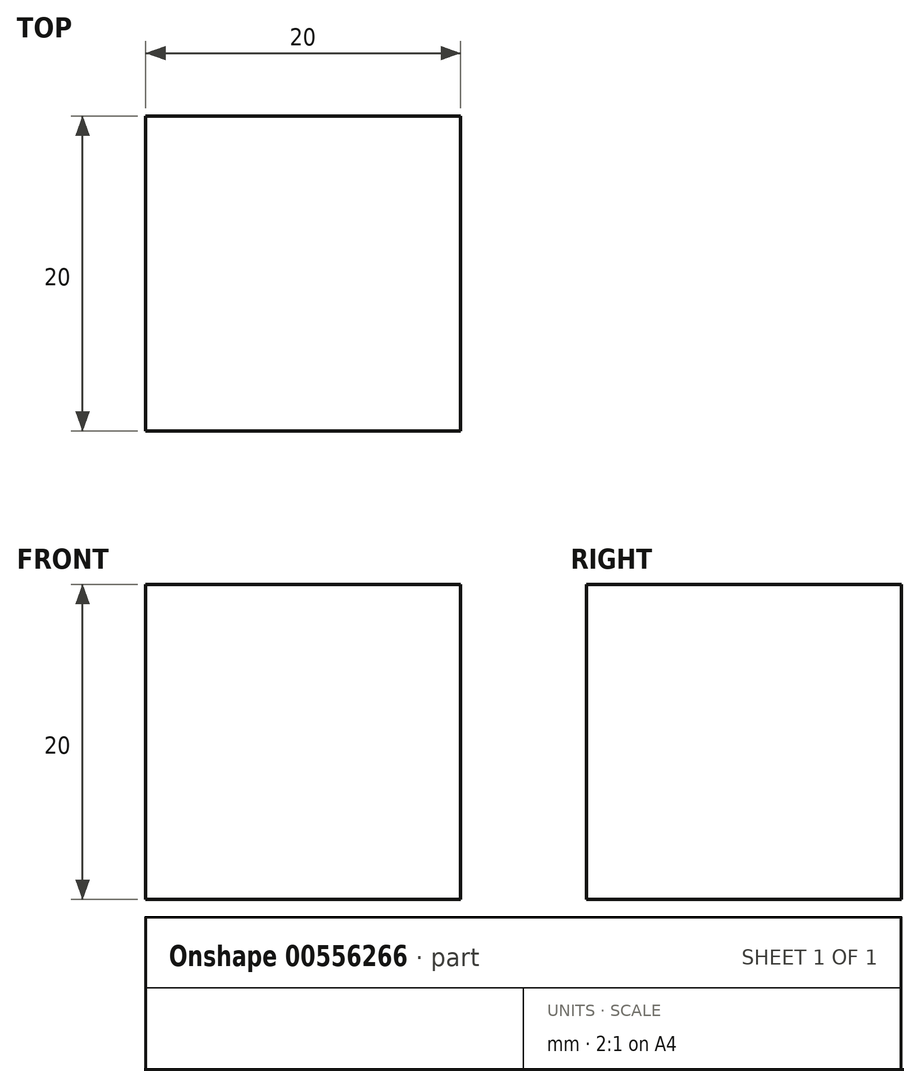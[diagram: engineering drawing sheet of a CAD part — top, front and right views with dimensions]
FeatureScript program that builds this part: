
annotation { "Feature Type Name" : "Feature", "Feature Type Description" : "" }
export const myFeature = defineFeature(function(context is Context, id is Id, definition is map)
    precondition{}
    {
        {
            var Q0;
            Q0=qCreatedBy(makeId("Top.planeOp"),FACE);
            var sketch = newSketch(context, id + "F0", { "sketchPlane" : qUnion([Q0])});
            skLineSegment(sketch, "E0.bottom", {"start": v(0, 0) * mm, "end": v(20, 0) * mm});
            skLineSegment(sketch, "E0.top", {"start": v(0, -20) * mm, "end": v(20, -20) * mm});
            skLineSegment(sketch, "E0.left", {"start": v(0, 0) * mm, "end": v(0, -20) * mm});
            skLineSegment(sketch, "E0.right", {"start": v(20, 0) * mm, "end": v(20, -20) * mm});
            skSolve(sketch);
        }
        {
            var Q0;
            Q0 = qSketchRegion(id + "F0", true);
            extrude(context, id + "F1", {"entities" : qUnion([Q0]), "depth" : 20 * mm, "offsetDistance" : 25 * mm});
        }
    });
